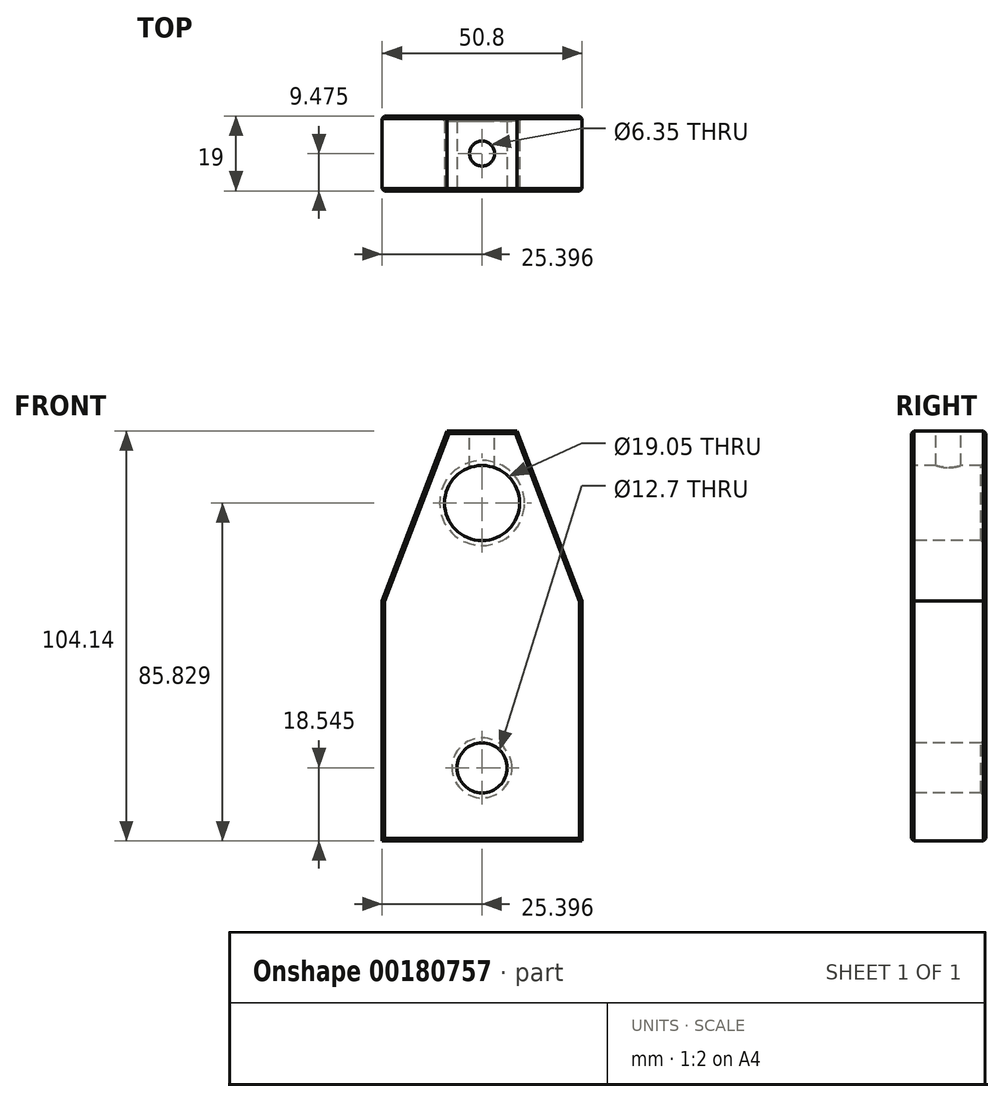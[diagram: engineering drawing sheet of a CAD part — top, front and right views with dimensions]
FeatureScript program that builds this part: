
annotation { "Feature Type Name" : "Feature", "Feature Type Description" : "" }
export const myFeature = defineFeature(function(context is Context, id is Id, definition is map)
    precondition{}
    {
        {
            var Q0;
            Q0=qCreatedBy(makeId("Front.planeOp"),FACE);
            var sketch = newSketch(context, id + "F0", { "sketchPlane" : qUnion([Q0])});
            skLineSegment(sketch, "E0", {"start": v(-10, 26.05) * mm, "end": v(7.79, 26.05) * mm});
            skLineSegment(sketch, "E1", {"start": v(7.79, 26.05) * mm, "end": v(24.3, -17.13) * mm});
            skLineSegment(sketch, "E2", {"start": v(24.3, -17.13) * mm, "end": v(24.3, -78.09) * mm});
            skLineSegment(sketch, "E3", {"start": v(24.3, -78.09) * mm, "end": v(-26.5, -78.09) * mm});
            skLineSegment(sketch, "E4", {"start": v(-26.5, -78.09) * mm, "end": v(-26.5, -17.13) * mm});
            skLineSegment(sketch, "E5", {"start": v(-26.5, -17.13) * mm, "end": v(-10, 26.05) * mm});
            skSolve(sketch);
        }
        {
            var Q0;
            Q0 = qSketchRegion(id + "F0", true);
            extrude(context, id + "F1", {"entities" : qUnion([Q0]), "depth" : 19 * mm});
        }
        {
            var Q0;
            Q0=makeQuery(id+"F1.opExtrude","CAP_FACE",FACE,{"disambiguationData":[OSD([sQuery(id+"F0.wireOp",EDGE,"E0"),sQuery(id+"F0.wireOp",EDGE,"E1"),sQuery(id+"F0.wireOp",EDGE,"E2"),sQuery(id+"F0.wireOp",EDGE,"E3"),sQuery(id+"F0.wireOp",EDGE,"E4"),sQuery(id+"F0.wireOp",EDGE,"E5")])],"isStart":false});
            var sketch = newSketch(context, id + "F2", { "sketchPlane" : qUnion([Q0])});
            skCircle(sketch, "E6", {"center": v(-1.1, 7.74) * mm, "radius": 9.53 * mm});
            skSolve(sketch);
        }
        {
            var Q0;
            Q0 = qSketchRegion(id + "F2", true);
            extrude(context, id + "F3", {"entities" : qUnion([Q0]), "operationType" : NewBodyOperationType.REMOVE, "oppositeDirection" : true, "depth" : 25.4 * mm});
        }
        {
            var Q0;
            Q0=makeQuery(id+"F1.opExtrude","CAP_FACE",FACE,{"disambiguationData":[OSD([sQuery(id+"F0.wireOp",EDGE,"E0"),sQuery(id+"F0.wireOp",EDGE,"E1"),sQuery(id+"F0.wireOp",EDGE,"E2"),sQuery(id+"F0.wireOp",EDGE,"E3"),sQuery(id+"F0.wireOp",EDGE,"E4"),sQuery(id+"F0.wireOp",EDGE,"E5")])],"isStart":false});
            var sketch = newSketch(context, id + "F4", { "sketchPlane" : qUnion([Q0])});
            skCircle(sketch, "E7", {"center": v(-1.1, -59.55) * mm, "radius": 6.35 * mm});
            skSolve(sketch);
        }
        {
            var Q0;
            Q0 = qSketchRegion(id + "F4", true);
            extrude(context, id + "F5", {"entities" : qUnion([Q0]), "operationType" : NewBodyOperationType.REMOVE, "oppositeDirection" : true, "depth" : 25.4 * mm});
        }
        {
            var Q0;
            Q0=makeQuery(id+"F1.opExtrude","SWEPT_FACE",FACE,{"disambiguationData":[OSD([sQuery(id+"F0.wireOp",EDGE,"E0")])]});
            var sketch = newSketch(context, id + "F6", { "sketchPlane" : qUnion([Q0])});
            skCircle(sketch, "E8", {"center": v(-1.1, -9.53) * mm, "radius": 3.18 * mm});
            skSolve(sketch);
        }
        {
            var Q0;
            Q0 = qSketchRegion(id + "F6", true);
            extrude(context, id + "F7", {"entities" : qUnion([Q0]), "operationType" : NewBodyOperationType.REMOVE, "oppositeDirection" : true, "depth" : 12.7 * mm});
        }
        {
            var Q0;
            Q0=makeQuery(id+"F3.boolean.opBoolean","COPY",EDGE,{"derivedFrom":makeQuery(id+"F3.opExtrude","CAP_EDGE",EDGE,{"disambiguationData":[OSD([sQuery(id+"F2.wireOp",EDGE,"E6")])],"isStart":true})});
            var Q1;
            Q1=makeQuery(id+"F5.boolean.opBoolean","COPY",EDGE,{"derivedFrom":makeQuery(id+"F5.opExtrude","CAP_EDGE",EDGE,{"disambiguationData":[OSD([sQuery(id+"F4.wireOp",EDGE,"E7")])],"isStart":true})});
            var Q2;
            Q2=makeQuery(id+"F3.boolean.opBoolean","INTERSECT",EDGE,{"derivedFrom":[makeQuery(id+"F1.opExtrude","CAP_FACE",FACE,{"disambiguationData":[OSD([sQuery(id+"F0.wireOp",EDGE,"E0"),sQuery(id+"F0.wireOp",EDGE,"E1"),sQuery(id+"F0.wireOp",EDGE,"E2"),sQuery(id+"F0.wireOp",EDGE,"E3"),sQuery(id+"F0.wireOp",EDGE,"E4"),sQuery(id+"F0.wireOp",EDGE,"E5")])],"isStart":true}),makeQuery(id+"F3.opExtrude","SWEPT_FACE",FACE,{"disambiguationData":[OSD([sQuery(id+"F2.wireOp",EDGE,"E6")])]})]});
            var Q3;
            Q3=makeQuery(id+"F5.boolean.opBoolean","INTERSECT",EDGE,{"derivedFrom":[makeQuery(id+"F1.opExtrude","CAP_FACE",FACE,{"disambiguationData":[OSD([sQuery(id+"F0.wireOp",EDGE,"E0"),sQuery(id+"F0.wireOp",EDGE,"E1"),sQuery(id+"F0.wireOp",EDGE,"E2"),sQuery(id+"F0.wireOp",EDGE,"E3"),sQuery(id+"F0.wireOp",EDGE,"E4"),sQuery(id+"F0.wireOp",EDGE,"E5")])],"isStart":true}),makeQuery(id+"F5.opExtrude","SWEPT_FACE",FACE,{"disambiguationData":[OSD([sQuery(id+"F4.wireOp",EDGE,"E7")])]})]});
            chamfer(context, id + "F8", {"entities" : qUnion([Q0, Q1, Q2, Q3]), "chamferType" : ChamferType.OFFSET_ANGLE, "width" : 1.27 * mm, "oppositeDirection" : false, "angle" : 45 * degree, "tangentPropagation" : true});
        }
        {
            var Q0;
            Q0=makeQuery(id+"F1.opExtrude","CAP_EDGE",EDGE,{"disambiguationData":[OSD([sQuery(id+"F0.wireOp",EDGE,"E5")])],"isStart":true});
            var Q1;
            Q1=makeQuery(id+"F1.opExtrude","CAP_EDGE",EDGE,{"disambiguationData":[OSD([sQuery(id+"F0.wireOp",EDGE,"E4")])],"isStart":true});
            var Q2;
            Q2=makeQuery(id+"F1.opExtrude","CAP_EDGE",EDGE,{"disambiguationData":[OSD([sQuery(id+"F0.wireOp",EDGE,"E3")])],"isStart":true});
            var Q3;
            Q3=makeQuery(id+"F1.opExtrude","CAP_EDGE",EDGE,{"disambiguationData":[OSD([sQuery(id+"F0.wireOp",EDGE,"E2")])],"isStart":true});
            var Q4;
            Q4=makeQuery(id+"F1.opExtrude","CAP_EDGE",EDGE,{"disambiguationData":[OSD([sQuery(id+"F0.wireOp",EDGE,"E1")])],"isStart":true});
            var Q5;
            Q5=makeQuery(id+"F1.opExtrude","CAP_EDGE",EDGE,{"disambiguationData":[OSD([sQuery(id+"F0.wireOp",EDGE,"E0")])],"isStart":true});
            var Q6;
            Q6=makeQuery(id+"F1.opExtrude","CAP_EDGE",EDGE,{"disambiguationData":[OSD([sQuery(id+"F0.wireOp",EDGE,"E4")])],"isStart":false});
            var Q7;
            Q7=makeQuery(id+"F1.opExtrude","CAP_EDGE",EDGE,{"disambiguationData":[OSD([sQuery(id+"F0.wireOp",EDGE,"E3")])],"isStart":false});
            var Q8;
            Q8=makeQuery(id+"F1.opExtrude","CAP_EDGE",EDGE,{"disambiguationData":[OSD([sQuery(id+"F0.wireOp",EDGE,"E2")])],"isStart":false});
            var Q9;
            Q9=makeQuery(id+"F1.opExtrude","CAP_EDGE",EDGE,{"disambiguationData":[OSD([sQuery(id+"F0.wireOp",EDGE,"E1")])],"isStart":false});
            var Q10;
            Q10=makeQuery(id+"F1.opExtrude","CAP_EDGE",EDGE,{"disambiguationData":[OSD([sQuery(id+"F0.wireOp",EDGE,"E0")])],"isStart":false});
            var Q11;
            Q11=makeQuery(id+"F1.opExtrude","CAP_EDGE",EDGE,{"disambiguationData":[OSD([sQuery(id+"F0.wireOp",EDGE,"E5")])],"isStart":false});
            chamfer(context, id + "F9", {"entities" : qUnion([Q0, Q1, Q2, Q3, Q4, Q5, Q6, Q7, Q8, Q9, Q10, Q11]), "width" : 0.64 * mm, "tangentPropagation" : true});
        }
    });
